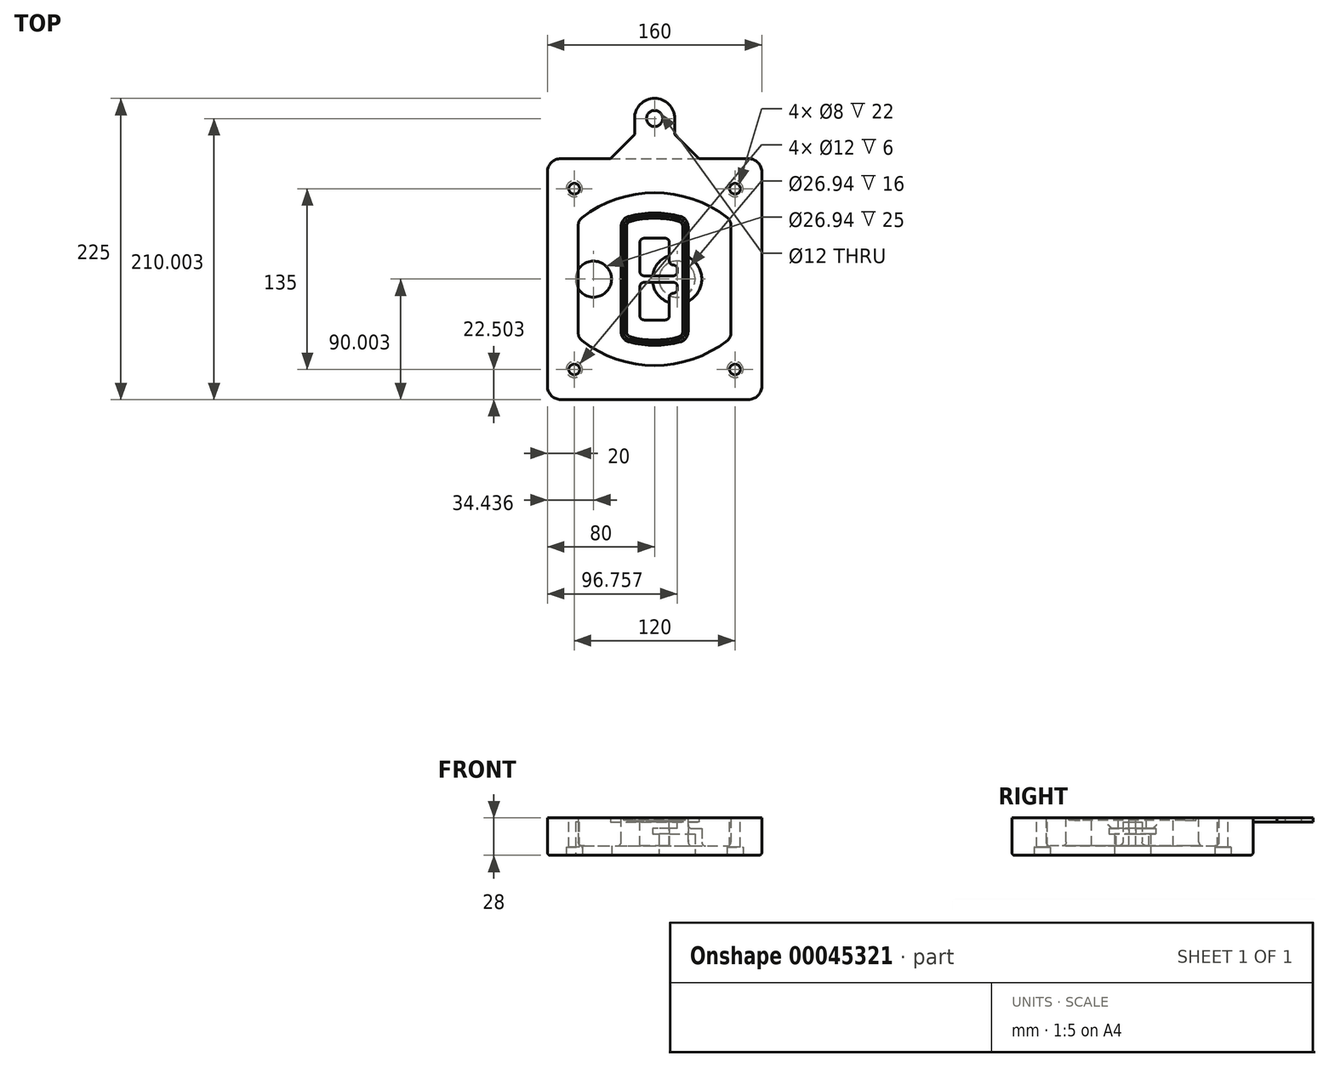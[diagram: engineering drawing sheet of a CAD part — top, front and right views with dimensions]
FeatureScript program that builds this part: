
annotation { "Feature Type Name" : "Feature", "Feature Type Description" : "" }
export const myFeature = defineFeature(function(context is Context, id is Id, definition is map)
    precondition{}
    {
        {
            var Q0;
            Q0=qCreatedBy(makeId("Top.planeOp"),FACE);
            var sketch = newSketch(context, id + "F0", { "sketchPlane" : qUnion([Q0])});
            skPoint(sketch, "E0.rect.middle", {"position": v(0, 0) * mm});
            skLineSegment(sketch, "E1.bottom", {"start": v(24.05, 28.38) * mm, "end": v(164.05, 28.38) * mm});
            skLineSegment(sketch, "E1.top", {"start": v(24.05, 208.38) * mm, "end": v(164.05, 208.38) * mm});
            skLineSegment(sketch, "E1.left", {"start": v(14.05, 38.38) * mm, "end": v(14.05, 198.38) * mm});
            skLineSegment(sketch, "E1.right", {"start": v(174.05, 38.38) * mm, "end": v(174.05, 198.38) * mm});
            skLineSegment(sketch, "E2", {"start": v(14.05, 208.38) * mm, "end": v(174.05, 28.38) * mm, "construction": true});
            skLineSegment(sketch, "E3", {"start": v(174.05, 208.38) * mm, "end": v(14.05, 28.38) * mm, "construction": true});
            skCircle(sketch, "E4", {"center": v(34.05, 185.88) * mm, "radius": 4 * mm});
            skCircle(sketch, "E5", {"center": v(154.05, 185.88) * mm, "radius": 4 * mm});
            skCircle(sketch, "E6", {"center": v(154.05, 50.88) * mm, "radius": 4 * mm});
            skCircle(sketch, "E7", {"center": v(34.05, 50.88) * mm, "radius": 4 * mm});
            skLineSegment(sketch, "E8", {"start": v(34.05, 185.88) * mm, "end": v(154.05, 185.88) * mm, "construction": true});
            skLineSegment(sketch, "E9", {"start": v(154.05, 185.88) * mm, "end": v(154.05, 50.88) * mm, "construction": true});
            skLineSegment(sketch, "E10", {"start": v(154.05, 50.88) * mm, "end": v(34.05, 50.88) * mm, "construction": true});
            skLineSegment(sketch, "E11", {"start": v(34.05, 50.88) * mm, "end": v(34.05, 185.88) * mm, "construction": true});
            skLineSegment(sketch, "E12", {"start": v(34.05, 158.68) * mm, "end": v(34.05, 78.09) * mm});
            skLineSegment(sketch, "E13", {"start": v(154.05, 158.68) * mm, "end": v(154.05, 78.09) * mm});
            skArc(sketch, "E14", {"start": v(150.2, 166.56) * mm, "mid": v(94.05, 185.88) * mm, "end": v(37.9, 166.56) * mm});
            skArc(sketch, "E15", {"start": v(37.9, 70.2) * mm, "mid": v(94.05, 50.88) * mm, "end": v(150.2, 70.2) * mm});
            skLineSegment(sketch, "E16", {"start": v(34.05, 118.38) * mm, "end": v(154.05, 118.38) * mm, "construction": true});
            skPoint(sketch, "E17.visualSharp", {"position": v(34.05, 73.38) * mm});
            skArc(sketch, "E17.filletArc", {"start": v(34.05, 78.09) * mm, "mid": v(35.06, 73.7) * mm, "end": v(37.9, 70.2) * mm});
            skPoint(sketch, "E18.visualSharp", {"position": v(34.05, 163.38) * mm});
            skArc(sketch, "E18.filletArc", {"start": v(37.9, 166.56) * mm, "mid": v(35.06, 163.06) * mm, "end": v(34.05, 158.68) * mm});
            skPoint(sketch, "E19.visualSharp", {"position": v(154.05, 163.38) * mm});
            skArc(sketch, "E19.filletArc", {"start": v(154.05, 158.68) * mm, "mid": v(153.04, 163.06) * mm, "end": v(150.2, 166.56) * mm});
            skPoint(sketch, "E20.visualSharp", {"position": v(154.05, 73.38) * mm});
            skArc(sketch, "E20.filletArc", {"start": v(150.2, 70.2) * mm, "mid": v(153.04, 73.7) * mm, "end": v(154.05, 78.09) * mm});
            skPoint(sketch, "E21.visualSharp", {"position": v(14.05, 208.38) * mm});
            skArc(sketch, "E21.filletArc", {"start": v(24.05, 208.38) * mm, "mid": v(16.98, 205.45) * mm, "end": v(14.05, 198.38) * mm});
            skPoint(sketch, "E22.visualSharp", {"position": v(174.05, 208.38) * mm});
            skArc(sketch, "E22.filletArc", {"start": v(174.05, 198.38) * mm, "mid": v(171.12, 205.45) * mm, "end": v(164.05, 208.38) * mm});
            skPoint(sketch, "E23.visualSharp", {"position": v(174.05, 28.38) * mm});
            skArc(sketch, "E23.filletArc", {"start": v(164.05, 28.38) * mm, "mid": v(171.12, 31.31) * mm, "end": v(174.05, 38.38) * mm});
            skPoint(sketch, "E24.visualSharp", {"position": v(14.05, 28.38) * mm});
            skArc(sketch, "E24.filletArc", {"start": v(14.05, 38.38) * mm, "mid": v(16.98, 31.31) * mm, "end": v(24.05, 28.38) * mm});
            skArc(sketch, "E25.0", {"start": v(151.05, 158.68) * mm, "mid": v(150.34, 161.75) * mm, "end": v(148.36, 164.2) * mm});
            skLineSegment(sketch, "E25.1", {"start": v(151.05, 158.68) * mm, "end": v(151.05, 78.09) * mm});
            skArc(sketch, "E25.2", {"start": v(148.36, 72.57) * mm, "mid": v(150.34, 75.02) * mm, "end": v(151.05, 78.09) * mm});
            skArc(sketch, "E25.3", {"start": v(39.74, 72.57) * mm, "mid": v(94.05, 53.88) * mm, "end": v(148.36, 72.57) * mm});
            skArc(sketch, "E25.4", {"start": v(37.05, 78.09) * mm, "mid": v(37.76, 75.02) * mm, "end": v(39.74, 72.57) * mm});
            skArc(sketch, "E25.5", {"start": v(148.36, 164.2) * mm, "mid": v(94.05, 182.88) * mm, "end": v(39.74, 164.2) * mm});
            skLineSegment(sketch, "E25.6", {"start": v(37.05, 158.68) * mm, "end": v(37.05, 78.09) * mm});
            skArc(sketch, "E25.7", {"start": v(39.74, 164.2) * mm, "mid": v(37.76, 161.75) * mm, "end": v(37.05, 158.68) * mm});
            skArc(sketch, "E26.0", {"start": v(35.43, 169.71) * mm, "mid": v(31.47, 164.82) * mm, "end": v(30.05, 158.68) * mm});
            skArc(sketch, "E26.1", {"start": v(152.67, 169.71) * mm, "mid": v(94.05, 189.88) * mm, "end": v(35.43, 169.71) * mm});
            skArc(sketch, "E26.2", {"start": v(158.05, 158.68) * mm, "mid": v(156.63, 164.82) * mm, "end": v(152.67, 169.71) * mm});
            skLineSegment(sketch, "E26.3", {"start": v(158.05, 158.68) * mm, "end": v(158.05, 78.09) * mm});
            skArc(sketch, "E26.4", {"start": v(152.67, 67.05) * mm, "mid": v(156.63, 71.95) * mm, "end": v(158.05, 78.09) * mm});
            skLineSegment(sketch, "E26.5", {"start": v(30.05, 158.68) * mm, "end": v(30.05, 78.09) * mm});
            skArc(sketch, "E26.6", {"start": v(35.43, 67.05) * mm, "mid": v(94.05, 46.88) * mm, "end": v(152.67, 67.05) * mm});
            skArc(sketch, "E26.7", {"start": v(30.05, 78.09) * mm, "mid": v(31.47, 71.95) * mm, "end": v(35.43, 67.05) * mm});
            skSolve(sketch);
        }
        {
            var Q0;
            Q0=makeQuery(id+"F0.imprint","IMPRINT",FACE,{"disambiguationData":[TD([[makeQuery(id+"F0.imprint","IMPRINT",EDGE,{"derivedFrom":sQuery(id+"F0.wireOp",EDGE,"E1.bottom")}),1.0]])]});
            var Q1;
            Q1=makeQuery(id+"F0.imprint","IMPRINT",FACE,{"disambiguationData":[TD([[makeQuery(id+"F0.imprint","IMPRINT",EDGE,{"derivedFrom":sQuery(id+"F0.wireOp",EDGE,"E12")}),1.0]])]});
            var Q2;
            Q2=makeQuery(id+"F0.imprint","IMPRINT",FACE,{"disambiguationData":[TD([[makeQuery(id+"F0.imprint","IMPRINT",EDGE,{"derivedFrom":sQuery(id+"F0.wireOp",EDGE,"E25.0")}),1.0]])]});
            var Q3;
            Q3=makeQuery(id+"F0.imprint","IMPRINT",FACE,{"disambiguationData":[TD([[makeQuery(id+"F0.imprint","IMPRINT",EDGE,{"derivedFrom":sQuery(id+"F0.wireOp",EDGE,"E12")}),-1.0]])]});
            extrude(context, id + "F1", {"entities" : qUnion([Q0, Q1, Q2, Q3]), "oppositeDirection" : true, "depth" : 25 * mm});
        }
        {
            var Q0;
            Q0=makeQuery(id+"F0.imprint","IMPRINT",FACE,{"disambiguationData":[TD([[makeQuery(id+"F0.imprint","IMPRINT",EDGE,{"derivedFrom":sQuery(id+"F0.wireOp",EDGE,"E12")}),1.0]])]});
            extrude(context, id + "F2", {"entities" : qUnion([Q0]), "operationType" : NewBodyOperationType.ADD, "depth" : 3 * mm});
        }
        {
            var Q0;
            Q0=makeQuery(id+"F0.imprint","IMPRINT",FACE,{"disambiguationData":[TD([[makeQuery(id+"F0.imprint","IMPRINT",EDGE,{"derivedFrom":sQuery(id+"F0.wireOp",EDGE,"E25.0")}),1.0]])]});
            extrude(context, id + "F3", {"entities" : qUnion([Q0]), "operationType" : NewBodyOperationType.REMOVE, "oppositeDirection" : true, "depth" : 18 * mm});
        }
        {
            var Q0;
            Q0=makeQuery(id+"F2.opExtrude","CAP_FACE",FACE,{"disambiguationData":[OSD([sQuery(id+"F0.wireOp",EDGE,"E12"),sQuery(id+"F0.wireOp",EDGE,"E13"),sQuery(id+"F0.wireOp",EDGE,"E14"),sQuery(id+"F0.wireOp",EDGE,"E15"),sQuery(id+"F0.wireOp",EDGE,"E17.filletArc"),sQuery(id+"F0.wireOp",EDGE,"E18.filletArc"),sQuery(id+"F0.wireOp",EDGE,"E19.filletArc"),sQuery(id+"F0.wireOp",EDGE,"E20.filletArc"),sQuery(id+"F0.wireOp",EDGE,"E25.0"),sQuery(id+"F0.wireOp",EDGE,"E25.1"),sQuery(id+"F0.wireOp",EDGE,"E25.2"),sQuery(id+"F0.wireOp",EDGE,"E25.3"),sQuery(id+"F0.wireOp",EDGE,"E25.4"),sQuery(id+"F0.wireOp",EDGE,"E25.5"),sQuery(id+"F0.wireOp",EDGE,"E25.6"),sQuery(id+"F0.wireOp",EDGE,"E25.7")])],"isStart":false});
            var sketch = newSketch(context, id + "F4", { "sketchPlane" : qUnion([Q0])});
            skArc(sketch, "E27.0", {"start": v(74.97, 71.41) * mm, "mid": v(94.05, 68.88) * mm, "end": v(113.13, 71.41) * mm});
            skArc(sketch, "E28.0", {"start": v(113.13, 165.35) * mm, "mid": v(94.05, 167.88) * mm, "end": v(74.97, 165.35) * mm});
            skLineSegment(sketch, "E29", {"start": v(69.05, 157.63) * mm, "end": v(69.05, 79.14) * mm});
            skLineSegment(sketch, "E30", {"start": v(119.05, 157.63) * mm, "end": v(119.05, 79.14) * mm});
            skLineSegment(sketch, "E31", {"start": v(69.05, 163.48) * mm, "end": v(119.05, 163.48) * mm, "construction": true});
            skLineSegment(sketch, "E32", {"start": v(69.05, 73.28) * mm, "end": v(119.05, 73.28) * mm, "construction": true});
            skPoint(sketch, "E33.visualSharp", {"position": v(69.05, 163.48) * mm});
            skArc(sketch, "E33.filletArc", {"start": v(74.97, 165.35) * mm, "mid": v(70.7, 162.5) * mm, "end": v(69.05, 157.63) * mm});
            skPoint(sketch, "E34.visualSharp", {"position": v(119.05, 163.48) * mm});
            skArc(sketch, "E34.filletArc", {"start": v(119.05, 157.63) * mm, "mid": v(117.4, 162.5) * mm, "end": v(113.13, 165.35) * mm});
            skPoint(sketch, "E35.visualSharp", {"position": v(119.05, 73.28) * mm});
            skArc(sketch, "E35.filletArc", {"start": v(113.13, 71.41) * mm, "mid": v(117.4, 74.27) * mm, "end": v(119.05, 79.14) * mm});
            skPoint(sketch, "E36.visualSharp", {"position": v(69.05, 73.28) * mm});
            skArc(sketch, "E36.filletArc", {"start": v(69.05, 79.14) * mm, "mid": v(70.7, 74.27) * mm, "end": v(74.97, 71.41) * mm});
            skArc(sketch, "E37.0", {"start": v(148.36, 164.2) * mm, "mid": v(94.05, 182.88) * mm, "end": v(39.74, 164.2) * mm});
            skArc(sketch, "E37.1", {"start": v(39.74, 164.2) * mm, "mid": v(37.76, 161.75) * mm, "end": v(37.05, 158.68) * mm});
            skLineSegment(sketch, "E37.2", {"start": v(37.05, 158.68) * mm, "end": v(37.05, 78.09) * mm});
            skArc(sketch, "E37.3", {"start": v(37.05, 78.09) * mm, "mid": v(37.76, 75.02) * mm, "end": v(39.74, 72.57) * mm});
            skArc(sketch, "E37.4", {"start": v(39.74, 72.57) * mm, "mid": v(94.05, 53.88) * mm, "end": v(148.36, 72.57) * mm});
            skArc(sketch, "E37.5", {"start": v(148.36, 72.57) * mm, "mid": v(150.34, 75.02) * mm, "end": v(151.05, 78.09) * mm});
            skLineSegment(sketch, "E37.6", {"start": v(151.05, 158.68) * mm, "end": v(151.05, 78.09) * mm});
            skArc(sketch, "E37.7", {"start": v(151.05, 158.68) * mm, "mid": v(150.34, 161.75) * mm, "end": v(148.36, 164.2) * mm});
            skLineSegment(sketch, "E38.0", {"start": v(117.05, 157.63) * mm, "end": v(117.05, 79.14) * mm});
            skArc(sketch, "E38.1", {"start": v(112.61, 73.34) * mm, "mid": v(115.81, 75.49) * mm, "end": v(117.05, 79.14) * mm});
            skArc(sketch, "E38.2", {"start": v(75.49, 73.34) * mm, "mid": v(94.05, 70.88) * mm, "end": v(112.61, 73.34) * mm});
            skArc(sketch, "E38.3", {"start": v(71.05, 79.14) * mm, "mid": v(72.29, 75.49) * mm, "end": v(75.49, 73.34) * mm});
            skLineSegment(sketch, "E38.4", {"start": v(71.05, 157.63) * mm, "end": v(71.05, 79.14) * mm});
            skArc(sketch, "E38.5", {"start": v(117.05, 157.63) * mm, "mid": v(115.81, 161.28) * mm, "end": v(112.61, 163.42) * mm});
            skArc(sketch, "E38.6", {"start": v(75.49, 163.42) * mm, "mid": v(72.29, 161.28) * mm, "end": v(71.05, 157.63) * mm});
            skArc(sketch, "E38.7", {"start": v(112.61, 163.42) * mm, "mid": v(94.05, 165.88) * mm, "end": v(75.49, 163.42) * mm});
            skArc(sketch, "E39.0", {"start": v(115.05, 157.63) * mm, "mid": v(114.23, 160.06) * mm, "end": v(112.1, 161.5) * mm});
            skLineSegment(sketch, "E39.1", {"start": v(115.05, 157.63) * mm, "end": v(115.05, 79.14) * mm});
            skArc(sketch, "E39.2", {"start": v(112.1, 75.27) * mm, "mid": v(114.23, 76.7) * mm, "end": v(115.05, 79.14) * mm});
            skArc(sketch, "E39.3", {"start": v(76, 75.27) * mm, "mid": v(94.05, 72.88) * mm, "end": v(112.1, 75.27) * mm});
            skArc(sketch, "E39.4", {"start": v(73.05, 79.14) * mm, "mid": v(73.87, 76.7) * mm, "end": v(76, 75.27) * mm});
            skArc(sketch, "E39.5", {"start": v(112.1, 161.5) * mm, "mid": v(94.05, 163.88) * mm, "end": v(76, 161.5) * mm});
            skLineSegment(sketch, "E39.6", {"start": v(73.05, 157.63) * mm, "end": v(73.05, 79.14) * mm});
            skArc(sketch, "E39.7", {"start": v(76, 161.5) * mm, "mid": v(73.87, 160.06) * mm, "end": v(73.05, 157.63) * mm});
            skLineSegment(sketch, "E40", {"start": v(69.05, 118.38) * mm, "end": v(119.05, 118.38) * mm, "construction": true});
            skLineSegment(sketch, "E41", {"start": v(83.05, 123.88) * mm, "end": v(83.05, 145.88) * mm});
            skLineSegment(sketch, "E42", {"start": v(86.05, 148.88) * mm, "end": v(102.05, 148.88) * mm});
            skLineSegment(sketch, "E43", {"start": v(105.05, 145.88) * mm, "end": v(105.05, 131.88) * mm});
            skLineSegment(sketch, "E44", {"start": v(108.05, 128.88) * mm, "end": v(108.05, 128.88) * mm});
            skLineSegment(sketch, "E45", {"start": v(111.05, 125.88) * mm, "end": v(111.05, 123.88) * mm});
            skLineSegment(sketch, "E46", {"start": v(108.05, 120.88) * mm, "end": v(86.05, 120.88) * mm});
            skPoint(sketch, "E47.visualSharp", {"position": v(83.05, 148.88) * mm});
            skArc(sketch, "E47.filletArc", {"start": v(86.05, 148.88) * mm, "mid": v(83.93, 148) * mm, "end": v(83.05, 145.88) * mm});
            skPoint(sketch, "E48.visualSharp", {"position": v(105.05, 148.88) * mm});
            skArc(sketch, "E48.filletArc", {"start": v(105.05, 145.88) * mm, "mid": v(104.17, 148) * mm, "end": v(102.05, 148.88) * mm});
            skPoint(sketch, "E49.visualSharp", {"position": v(105.05, 128.88) * mm});
            skArc(sketch, "E49.filletArc", {"start": v(105.05, 131.88) * mm, "mid": v(105.93, 129.76) * mm, "end": v(108.05, 128.88) * mm});
            skPoint(sketch, "E50.visualSharp", {"position": v(111.05, 128.88) * mm});
            skArc(sketch, "E50.filletArc", {"start": v(111.05, 125.88) * mm, "mid": v(110.17, 128) * mm, "end": v(108.05, 128.88) * mm});
            skPoint(sketch, "E51.visualSharp", {"position": v(111.05, 120.88) * mm});
            skArc(sketch, "E51.filletArc", {"start": v(108.05, 120.88) * mm, "mid": v(110.17, 121.76) * mm, "end": v(111.05, 123.88) * mm});
            skPoint(sketch, "E52.visualSharp", {"position": v(83.05, 120.88) * mm});
            skArc(sketch, "E52.filletArc", {"start": v(83.05, 123.88) * mm, "mid": v(83.93, 121.76) * mm, "end": v(86.05, 120.88) * mm});
            skLineSegment(sketch, "E53.0.MirrorCS", {"start": v(108.05, 115.88) * mm, "end": v(86.05, 115.88) * mm});
            skArc(sketch, "E54.0.MirrorCS", {"start": v(83.05, 112.88) * mm, "mid": v(83.93, 115) * mm, "end": v(86.05, 115.88) * mm});
            skLineSegment(sketch, "E55.0.MirrorCS", {"start": v(83.05, 112.88) * mm, "end": v(83.05, 90.88) * mm});
            skArc(sketch, "E56.0.MirrorCS", {"start": v(86.05, 87.88) * mm, "mid": v(83.93, 88.76) * mm, "end": v(83.05, 90.88) * mm});
            skLineSegment(sketch, "E57.0.MirrorCS", {"start": v(86.05, 87.88) * mm, "end": v(102.05, 87.88) * mm});
            skArc(sketch, "E58.0.MirrorCS", {"start": v(105.05, 90.88) * mm, "mid": v(104.17, 88.76) * mm, "end": v(102.05, 87.88) * mm});
            skLineSegment(sketch, "E59.0.MirrorCS", {"start": v(105.05, 90.88) * mm, "end": v(105.05, 104.88) * mm});
            skArc(sketch, "E60.0.MirrorCS", {"start": v(105.05, 104.88) * mm, "mid": v(105.93, 107) * mm, "end": v(108.05, 107.88) * mm});
            skArc(sketch, "E61.0.MirrorCS", {"start": v(111.05, 110.88) * mm, "mid": v(110.17, 108.76) * mm, "end": v(108.05, 107.88) * mm});
            skLineSegment(sketch, "E62.0.MirrorCS", {"start": v(111.05, 110.88) * mm, "end": v(111.05, 112.88) * mm});
            skArc(sketch, "E63.0.MirrorCS", {"start": v(108.05, 115.88) * mm, "mid": v(110.17, 115) * mm, "end": v(111.05, 112.88) * mm});
            skSolve(sketch);
        }
        {
            var Q0;
            Q0=makeQuery(id+"F4.imprint","IMPRINT",FACE,{"disambiguationData":[TD([[makeQuery(id+"F4.imprint","IMPRINT",EDGE,{"derivedFrom":sQuery(id+"F4.wireOp",EDGE,"E27.0")}),1.0]])]});
            var Q1;
            Q1=makeQuery(id+"F4.imprint","IMPRINT",FACE,{"disambiguationData":[TD([[makeQuery(id+"F4.imprint","IMPRINT",EDGE,{"derivedFrom":sQuery(id+"F4.wireOp",EDGE,"E38.0")}),-1.0]])]});
            var Q2;
            Q2=makeQuery(id+"F4.imprint","IMPRINT",FACE,{"disambiguationData":[TD([[makeQuery(id+"F4.imprint","IMPRINT",EDGE,{"derivedFrom":sQuery(id+"F4.wireOp",EDGE,"E39.0")}),1.0]])]});
            extrude(context, id + "F5", {"entities" : qUnion([Q0, Q1, Q2]), "operationType" : NewBodyOperationType.ADD, "endBound" : BoundingType.UP_TO_NEXT, "oppositeDirection" : true, "depth" : 25 * mm});
        }
        {
            var Q0;
            Q0=makeQuery(id+"F4.imprint","IMPRINT",FACE,{"disambiguationData":[TD([[makeQuery(id+"F4.imprint","IMPRINT",EDGE,{"derivedFrom":sQuery(id+"F4.wireOp",EDGE,"E38.0")}),-1.0]])]});
            extrude(context, id + "F6", {"entities" : qUnion([Q0]), "operationType" : NewBodyOperationType.REMOVE, "oppositeDirection" : true, "depth" : 2 * mm});
        }
        {
            var Q0;
            Q0=makeQuery(id+"F1.opExtrude","CAP_FACE",FACE,{"disambiguationData":[OSD([sQuery(id+"F0.wireOp",EDGE,"E1.bottom"),sQuery(id+"F0.wireOp",EDGE,"E1.top"),sQuery(id+"F0.wireOp",EDGE,"E1.left"),sQuery(id+"F0.wireOp",EDGE,"E1.right"),sQuery(id+"F0.wireOp",EDGE,"E4"),sQuery(id+"F0.wireOp",EDGE,"E5"),sQuery(id+"F0.wireOp",EDGE,"E6"),sQuery(id+"F0.wireOp",EDGE,"E7"),sQuery(id+"F0.wireOp",EDGE,"E21.filletArc"),sQuery(id+"F0.wireOp",EDGE,"E22.filletArc"),sQuery(id+"F0.wireOp",EDGE,"E23.filletArc"),sQuery(id+"F0.wireOp",EDGE,"E24.filletArc")])],"isStart":false});
            var sketch = newSketch(context, id + "F7", { "sketchPlane" : qUnion([Q0])});
            skCircle(sketch, "E64", {"center": v(110.8, -118.38) * mm, "radius": 13.47 * mm});
            skCircle(sketch, "E65", {"center": v(48.49, -118.38) * mm, "radius": 13.47 * mm});
            skLineSegment(sketch, "E66", {"start": v(174.05, -118.38) * mm, "end": v(14.05, -118.38) * mm});
            skCircle(sketch, "E67", {"center": v(110.8, -118.38) * mm, "radius": 18.47 * mm});
            skCircle(sketch, "E68", {"center": v(154.05, -185.88) * mm, "radius": 6 * mm});
            skCircle(sketch, "E69", {"center": v(34.05, -185.88) * mm, "radius": 6 * mm});
            skCircle(sketch, "E70", {"center": v(34.05, -50.88) * mm, "radius": 6 * mm});
            skCircle(sketch, "E71", {"center": v(154.05, -50.88) * mm, "radius": 6 * mm});
            skSolve(sketch);
        }
        {
            var Q0;
            {var subQ1=sQuery(id+"F7.wireOp",EDGE,"E66");var subQ4=sQuery(id+"F7.wireOp",EDGE,"E64");var subQ6=makeQuery(id+"F7.imprint","INTERSECT",VERTEX,{"disambiguationData":[OD(0.0)],"derivedFrom":[subQ4,subQ1]});Q0=makeQuery(id+"F7.imprint","IMPRINT",FACE,{"disambiguationData":[TD([[makeQuery(id+"F7.imprint","IMPRINT",EDGE,{"disambiguationData":[TD([[subQ6,-1.0]])],"derivedFrom":subQ4}),-1.0]])]});}
            var Q1;
            {var subQ0=sQuery(id+"F7.wireOp",EDGE,"E66");var subQ1=sQuery(id+"F7.wireOp",EDGE,"E64");var subQ3=makeQuery(id+"F7.imprint","INTERSECT",VERTEX,{"disambiguationData":[OD(0.0)],"derivedFrom":[subQ1,subQ0]});Q1=makeQuery(id+"F7.imprint","IMPRINT",FACE,{"disambiguationData":[TD([[makeQuery(id+"F7.imprint","IMPRINT",EDGE,{"disambiguationData":[TD([[subQ3,-1.0]])],"derivedFrom":subQ1}),1.0]])]});}
            var Q2;
            {var subQ0=sQuery(id+"F7.wireOp",EDGE,"E66");var subQ1=sQuery(id+"F7.wireOp",EDGE,"E64");var subQ3=makeQuery(id+"F7.imprint","INTERSECT",VERTEX,{"disambiguationData":[OD(0.0)],"derivedFrom":[subQ1,subQ0]});Q2=makeQuery(id+"F7.imprint","IMPRINT",FACE,{"disambiguationData":[TD([[makeQuery(id+"F7.imprint","IMPRINT",EDGE,{"disambiguationData":[TD([[subQ3,1.0]])],"derivedFrom":subQ1}),1.0]])]});}
            var Q3;
            {var subQ1=sQuery(id+"F7.wireOp",EDGE,"E66");var subQ4=sQuery(id+"F7.wireOp",EDGE,"E64");var subQ6=makeQuery(id+"F7.imprint","INTERSECT",VERTEX,{"disambiguationData":[OD(0.0)],"derivedFrom":[subQ4,subQ1]});Q3=makeQuery(id+"F7.imprint","IMPRINT",FACE,{"disambiguationData":[TD([[makeQuery(id+"F7.imprint","IMPRINT",EDGE,{"disambiguationData":[TD([[subQ6,1.0]])],"derivedFrom":subQ4}),-1.0]])]});}
            extrude(context, id + "F8", {"entities" : qUnion([Q0, Q1, Q2, Q3]), "operationType" : NewBodyOperationType.ADD, "oppositeDirection" : true, "depth" : 20 * mm});
        }
        {
            var Q0;
            {var subQ0=sQuery(id+"F7.wireOp",EDGE,"E66");var subQ1=sQuery(id+"F7.wireOp",EDGE,"E64");var subQ3=makeQuery(id+"F7.imprint","INTERSECT",VERTEX,{"disambiguationData":[OD(0.0)],"derivedFrom":[subQ1,subQ0]});Q0=makeQuery(id+"F7.imprint","IMPRINT",FACE,{"disambiguationData":[TD([[makeQuery(id+"F7.imprint","IMPRINT",EDGE,{"disambiguationData":[TD([[subQ3,-1.0]])],"derivedFrom":subQ1}),1.0]])]});}
            var Q1;
            {var subQ0=sQuery(id+"F7.wireOp",EDGE,"E66");var subQ1=sQuery(id+"F7.wireOp",EDGE,"E64");var subQ3=makeQuery(id+"F7.imprint","INTERSECT",VERTEX,{"disambiguationData":[OD(0.0)],"derivedFrom":[subQ1,subQ0]});Q1=makeQuery(id+"F7.imprint","IMPRINT",FACE,{"disambiguationData":[TD([[makeQuery(id+"F7.imprint","IMPRINT",EDGE,{"disambiguationData":[TD([[subQ3,1.0]])],"derivedFrom":subQ1}),1.0]])]});}
            extrude(context, id + "F9", {"entities" : qUnion([Q0, Q1]), "operationType" : NewBodyOperationType.REMOVE, "oppositeDirection" : true, "depth" : 16 * mm});
        }
        {
            var Q0;
            {var subQ0=sQuery(id+"F7.wireOp",EDGE,"E66");var subQ1=sQuery(id+"F7.wireOp",EDGE,"E65");var subQ3=makeQuery(id+"F7.imprint","INTERSECT",VERTEX,{"disambiguationData":[OD(0.0)],"derivedFrom":[subQ1,subQ0]});Q0=makeQuery(id+"F7.imprint","IMPRINT",FACE,{"disambiguationData":[TD([[makeQuery(id+"F7.imprint","IMPRINT",EDGE,{"disambiguationData":[TD([[subQ3,-1.0]])],"derivedFrom":subQ1}),1.0]])]});}
            var Q1;
            {var subQ0=sQuery(id+"F7.wireOp",EDGE,"E66");var subQ1=sQuery(id+"F7.wireOp",EDGE,"E65");var subQ3=makeQuery(id+"F7.imprint","INTERSECT",VERTEX,{"disambiguationData":[OD(0.0)],"derivedFrom":[subQ1,subQ0]});Q1=makeQuery(id+"F7.imprint","IMPRINT",FACE,{"disambiguationData":[TD([[makeQuery(id+"F7.imprint","IMPRINT",EDGE,{"disambiguationData":[TD([[subQ3,1.0]])],"derivedFrom":subQ1}),1.0]])]});}
            extrude(context, id + "F10", {"entities" : qUnion([Q0, Q1]), "operationType" : NewBodyOperationType.REMOVE, "oppositeDirection" : true, "depth" : 25 * mm});
        }
        {
            var Q0;
            Q0=makeQuery(id+"F7.imprint","IMPRINT",FACE,{"disambiguationData":[TD([[makeQuery(id+"F7.imprint","IMPRINT",EDGE,{"derivedFrom":sQuery(id+"F7.wireOp",EDGE,"E68")}),1.0]])]});
            var Q1;
            Q1=makeQuery(id+"F7.imprint","IMPRINT",FACE,{"disambiguationData":[TD([[makeQuery(id+"F7.imprint","IMPRINT",EDGE,{"derivedFrom":makeQuery(id+"F1.opExtrude","CAP_EDGE",EDGE,{"disambiguationData":[OSD([sQuery(id+"F0.wireOp",EDGE,"E5")])],"isStart":false})}),-1.0]])]});
            var Q2;
            Q2=makeQuery(id+"F7.imprint","IMPRINT",FACE,{"disambiguationData":[TD([[makeQuery(id+"F7.imprint","IMPRINT",EDGE,{"derivedFrom":sQuery(id+"F7.wireOp",EDGE,"E69")}),1.0]])]});
            var Q3;
            Q3=makeQuery(id+"F7.imprint","IMPRINT",FACE,{"disambiguationData":[TD([[makeQuery(id+"F7.imprint","IMPRINT",EDGE,{"derivedFrom":makeQuery(id+"F1.opExtrude","CAP_EDGE",EDGE,{"disambiguationData":[OSD([sQuery(id+"F0.wireOp",EDGE,"E4")])],"isStart":false})}),-1.0]])]});
            var Q4;
            Q4=makeQuery(id+"F7.imprint","IMPRINT",FACE,{"disambiguationData":[TD([[makeQuery(id+"F7.imprint","IMPRINT",EDGE,{"derivedFrom":sQuery(id+"F7.wireOp",EDGE,"E70")}),1.0]])]});
            var Q5;
            Q5=makeQuery(id+"F7.imprint","IMPRINT",FACE,{"disambiguationData":[TD([[makeQuery(id+"F7.imprint","IMPRINT",EDGE,{"derivedFrom":makeQuery(id+"F1.opExtrude","CAP_EDGE",EDGE,{"disambiguationData":[OSD([sQuery(id+"F0.wireOp",EDGE,"E7")])],"isStart":false})}),-1.0]])]});
            var Q6;
            Q6=makeQuery(id+"F7.imprint","IMPRINT",FACE,{"disambiguationData":[TD([[makeQuery(id+"F7.imprint","IMPRINT",EDGE,{"derivedFrom":sQuery(id+"F7.wireOp",EDGE,"E71")}),1.0]])]});
            var Q7;
            Q7=makeQuery(id+"F7.imprint","IMPRINT",FACE,{"disambiguationData":[TD([[makeQuery(id+"F7.imprint","IMPRINT",EDGE,{"derivedFrom":makeQuery(id+"F1.opExtrude","CAP_EDGE",EDGE,{"disambiguationData":[OSD([sQuery(id+"F0.wireOp",EDGE,"E6")])],"isStart":false})}),-1.0]])]});
            extrude(context, id + "F11", {"entities" : qUnion([Q0, Q1, Q2, Q3, Q4, Q5, Q6, Q7]), "operationType" : NewBodyOperationType.REMOVE, "oppositeDirection" : true, "depth" : 6 * mm});
        }
        {
            var Q0;
            Q0=makeQuery(id+"F9.boolean.opBoolean","COPY",FACE,{"derivedFrom":makeQuery(id+"F9.opExtrude","CAP_FACE",FACE,{"disambiguationData":[OSD([sQuery(id+"F7.wireOp",EDGE,"E64")])],"isStart":false})});
            var sketch = newSketch(context, id + "F12", { "sketchPlane" : qUnion([Q0])});
            skArc(sketch, "E72.0", {"start": v(105.05, -100.83) * mm, "mid": v(96.62, -106.56) * mm, "end": v(92.5, -115.88) * mm});
            skArc(sketch, "E72.1", {"start": v(92.5, -120.88) * mm, "mid": v(96.62, -130.2) * mm, "end": v(105.05, -135.93) * mm});
            skLineSegment(sketch, "E73", {"start": v(92.5, -120.88) * mm, "end": v(108.05, -120.88) * mm});
            skLineSegment(sketch, "E74.0", {"start": v(108.05, -115.88) * mm, "end": v(92.5, -115.88) * mm});
            skArc(sketch, "E74.1", {"start": v(108.05, -115.88) * mm, "mid": v(110.17, -115) * mm, "end": v(111.05, -112.88) * mm});
            skLineSegment(sketch, "E74.2", {"start": v(111.05, -110.88) * mm, "end": v(111.05, -112.88) * mm});
            skArc(sketch, "E74.3", {"start": v(111.05, -110.88) * mm, "mid": v(110.17, -108.76) * mm, "end": v(108.05, -107.88) * mm});
            skArc(sketch, "E74.4", {"start": v(105.05, -104.88) * mm, "mid": v(105.93, -107) * mm, "end": v(108.05, -107.88) * mm});
            skLineSegment(sketch, "E74.5", {"start": v(105.05, -100.83) * mm, "end": v(105.05, -104.88) * mm});
            skLineSegment(sketch, "E74.7", {"start": v(108.05, -120.88) * mm, "end": v(92.5, -120.88) * mm});
            skArc(sketch, "E74.8", {"start": v(108.05, -120.88) * mm, "mid": v(110.17, -121.76) * mm, "end": v(111.05, -123.88) * mm});
            skLineSegment(sketch, "E74.9", {"start": v(111.05, -125.88) * mm, "end": v(111.05, -123.88) * mm});
            skArc(sketch, "E74.10", {"start": v(111.05, -125.88) * mm, "mid": v(110.17, -128) * mm, "end": v(108.05, -128.88) * mm});
            skArc(sketch, "E74.11", {"start": v(105.05, -131.88) * mm, "mid": v(105.93, -129.76) * mm, "end": v(108.05, -128.88) * mm});
            skLineSegment(sketch, "E74.12", {"start": v(105.05, -135.93) * mm, "end": v(105.05, -131.88) * mm});
            skPoint(sketch, "E75.orphan", {"position": v(105.05, -145.88) * mm});
            skPoint(sketch, "E76.orphan", {"position": v(86.05, -120.88) * mm});
            skPoint(sketch, "E77.orphan", {"position": v(86.05, -115.88) * mm});
            skPoint(sketch, "E78.orphan", {"position": v(105.05, -90.88) * mm});
            skSolve(sketch);
        }
        {
            var Q0;
            {var subQ7=sQuery(id+"F12.wireOp",EDGE,"E72.0");var subQ14=sQuery(id+"F12.wireOp",EDGE,"E72.1");var subQ16=sQuery(id+"F12.wireOp",EDGE,"E74.1");var subQ18=sQuery(id+"F12.wireOp",EDGE,"E74.8");Q0=qUnion([makeQuery(id+"F12.imprint","IMPRINT",FACE,{"disambiguationData":[TD([[makeQuery(id+"F12.imprint","IMPRINT",EDGE,{"derivedFrom":subQ7}),1.0]])]}),makeQuery(id+"F12.imprint","IMPRINT",FACE,{"disambiguationData":[TD([[makeQuery(id+"F12.imprint","IMPRINT",EDGE,{"derivedFrom":subQ14}),1.0]])]}),makeQuery(id+"F12.imprint","IMPRINT",FACE,{"disambiguationData":[TD([[makeQuery(id+"F12.imprint","IMPRINT",EDGE,{"derivedFrom":subQ16}),1.0]])]}),makeQuery(id+"F12.imprint","IMPRINT",FACE,{"disambiguationData":[TD([[makeQuery(id+"F12.imprint","IMPRINT",EDGE,{"derivedFrom":subQ18}),-1.0]])]})]);}
            var Q1;
            Q1=makeQuery(id+"F5.boolean.opBoolean","SPLIT",FACE,{"disambiguationData":[TD([makeQuery(id+"F5.opExtrude","SWEPT_FACE",FACE,{"disambiguationData":[OSD([sQuery(id+"F4.wireOp",EDGE,"E41")])]})])],"derivedFrom":makeQuery(id+"F3.boolean.opBoolean","COPY",FACE,{"derivedFrom":makeQuery(id+"F3.opExtrude","CAP_FACE",FACE,{"disambiguationData":[OSD([sQuery(id+"F0.wireOp",EDGE,"E25.0"),sQuery(id+"F0.wireOp",EDGE,"E25.1"),sQuery(id+"F0.wireOp",EDGE,"E25.2"),sQuery(id+"F0.wireOp",EDGE,"E25.3"),sQuery(id+"F0.wireOp",EDGE,"E25.4"),sQuery(id+"F0.wireOp",EDGE,"E25.5"),sQuery(id+"F0.wireOp",EDGE,"E25.6"),sQuery(id+"F0.wireOp",EDGE,"E25.7")])],"isStart":false})})});
            extrude(context, id + "F13", {"entities" : qUnion([Q0]), "operationType" : NewBodyOperationType.REMOVE, "endBound" : BoundingType.UP_TO_SURFACE, "endBoundEntityFace" : qUnion([Q1]), "depth" : 25 * mm});
        }
        {
            var Q0;
            Q0=makeQuery(id+"F3.boolean.opBoolean","COPY",EDGE,{"derivedFrom":makeQuery(id+"F3.opExtrude","CAP_EDGE",EDGE,{"disambiguationData":[OSD([sQuery(id+"F0.wireOp",EDGE,"E25.6")])],"isStart":false})});
            var Q1;
            Q1=makeQuery(id+"F8.boolean.opBoolean","INTERSECT",EDGE,{"derivedFrom":[makeQuery(id+"F5.opExtrude","SWEPT_FACE",FACE,{"disambiguationData":[OSD([sQuery(id+"F4.wireOp",EDGE,"E30")])]}),makeQuery(id+"F8.opExtrude","CAP_FACE",FACE,{"disambiguationData":[OSD([sQuery(id+"F7.wireOp",EDGE,"E67")])],"isStart":false})]});
            var Q2;
            Q2=makeQuery(id+"F8.boolean.opBoolean","INTERSECT",EDGE,{"disambiguationData":[OD(1.0)],"derivedFrom":[makeQuery(id+"F5.opExtrude","SWEPT_FACE",FACE,{"disambiguationData":[OSD([sQuery(id+"F4.wireOp",EDGE,"E30")])]}),makeQuery(id+"F8.opExtrude","SWEPT_FACE",FACE,{"disambiguationData":[OSD([sQuery(id+"F7.wireOp",EDGE,"E67")])]})]});
            var Q3;
            {var subQ0=sQuery(id+"F4.wireOp",EDGE,"E30");Q3=makeQuery(id+"F8.boolean.opBoolean","SPLIT",EDGE,{"disambiguationData":[TD([makeQuery(id+"F5.opExtrude","SWEPT_FACE",FACE,{"disambiguationData":[OSD([sQuery(id+"F4.wireOp",EDGE,"E35.filletArc")])]})])],"derivedFrom":makeQuery(id+"F5.opExtrude","CAP_EDGE",EDGE,{"disambiguationData":[OSD([subQ0])],"isStart":false})});}
            var Q4;
            {var subQ0=sQuery(id+"F0.wireOp",EDGE,"E25.7");var subQ1=sQuery(id+"F0.wireOp",EDGE,"E25.1");var subQ2=sQuery(id+"F0.wireOp",EDGE,"E25.6");var subQ3=sQuery(id+"F0.wireOp",EDGE,"E25.5");var subQ4=sQuery(id+"F0.wireOp",EDGE,"E25.4");var subQ5=sQuery(id+"F0.wireOp",EDGE,"E25.0");var subQ6=sQuery(id+"F0.wireOp",EDGE,"E25.2");var subQ7=sQuery(id+"F0.wireOp",EDGE,"E25.3");Q4=makeQuery(id+"F8.boolean.opBoolean","INTERSECT",EDGE,{"derivedFrom":[makeQuery(id+"F5.boolean.opBoolean","SPLIT",FACE,{"disambiguationData":[TD([makeQuery(id+"F2.opExtrude","SWEPT_FACE",FACE,{"disambiguationData":[OSD([subQ5])]})])],"derivedFrom":makeQuery(id+"F3.boolean.opBoolean","COPY",FACE,{"derivedFrom":makeQuery(id+"F3.opExtrude","CAP_FACE",FACE,{"disambiguationData":[OSD([subQ5,subQ1,subQ6,subQ7,subQ4,subQ3,subQ2,subQ0])],"isStart":false})})}),makeQuery(id+"F8.opExtrude","SWEPT_FACE",FACE,{"disambiguationData":[OSD([sQuery(id+"F7.wireOp",EDGE,"E67")])]})]});}
            var Q5;
            Q5=makeQuery(id+"F8.boolean.opBoolean","INTERSECT",EDGE,{"disambiguationData":[OD(0.0)],"derivedFrom":[makeQuery(id+"F5.opExtrude","SWEPT_FACE",FACE,{"disambiguationData":[OSD([sQuery(id+"F4.wireOp",EDGE,"E30")])]}),makeQuery(id+"F8.opExtrude","SWEPT_FACE",FACE,{"disambiguationData":[OSD([sQuery(id+"F7.wireOp",EDGE,"E67")])]})]});
            fillet(context, id + "F14", {"entities" : qUnion([Q0, Q1, Q2, Q3, Q4, Q5]), "radius" : 3 * mm, "tangentPropagation" : true, "allowEdgeOverflow" : false});
        }
        {
            var Q0;
            Q0=makeQuery(id+"F1.opExtrude","CAP_EDGE",EDGE,{"disambiguationData":[OSD([sQuery(id+"F0.wireOp",EDGE,"E1.bottom")])],"isStart":false});
            fillet(context, id + "F15", {"entities" : qUnion([Q0]), "radius" : 2 * mm, "tangentPropagation" : true, "allowEdgeOverflow" : false});
        }
        {
            var Q0;
            {var subQ0=sQuery(id+"F0.wireOp",EDGE,"E22.filletArc");var subQ1=sQuery(id+"F0.wireOp",EDGE,"E7");var subQ2=sQuery(id+"F0.wireOp",EDGE,"E6");var subQ3=sQuery(id+"F0.wireOp",EDGE,"E5");var subQ4=sQuery(id+"F0.wireOp",EDGE,"E4");var subQ5=sQuery(id+"F0.wireOp",EDGE,"E1.bottom");var subQ6=sQuery(id+"F0.wireOp",EDGE,"E21.filletArc");var subQ7=sQuery(id+"F0.wireOp",EDGE,"E1.top");var subQ8=sQuery(id+"F0.wireOp",EDGE,"E1.left");var subQ9=sQuery(id+"F0.wireOp",EDGE,"E1.right");var subQ10=sQuery(id+"F0.wireOp",EDGE,"E23.filletArc");var subQ11=sQuery(id+"F0.wireOp",EDGE,"E24.filletArc");Q0=makeQuery(id+"F2.boolean.opBoolean","SPLIT",FACE,{"disambiguationData":[TD([makeQuery(id+"F1.opExtrude","SWEPT_FACE",FACE,{"disambiguationData":[OSD([subQ5])]})])],"derivedFrom":makeQuery(id+"F1.opExtrude","CAP_FACE",FACE,{"disambiguationData":[OSD([subQ5,subQ7,subQ8,subQ9,subQ4,subQ3,subQ2,subQ1,subQ6,subQ0,subQ10,subQ11])],"isStart":true})});}
            var sketch = newSketch(context, id + "F16", { "sketchPlane" : qUnion([Q0])});
            skLineSegment(sketch, "E79", {"start": v(61.05, 208.38) * mm, "end": v(79.05, 226.38) * mm});
            skLineSegment(sketch, "E80", {"start": v(79.05, 226.38) * mm, "end": v(79.05, 238.38) * mm});
            skLineSegment(sketch, "E81", {"start": v(127.05, 208.38) * mm, "end": v(109.05, 226.38) * mm});
            skLineSegment(sketch, "E82", {"start": v(109.05, 226.38) * mm, "end": v(109.05, 238.38) * mm});
            skArc(sketch, "E83", {"start": v(109.05, 238.38) * mm, "mid": v(94.05, 253.38) * mm, "end": v(79.05, 238.38) * mm});
            skCircle(sketch, "E84", {"center": v(94.05, 238.38) * mm, "radius": 6 * mm});
            skLineSegment(sketch, "E85", {"start": v(94.05, 238.38) * mm, "end": v(94.05, 208.38) * mm, "construction": true});
            skLineSegment(sketch, "E86", {"start": v(14.05, 118.38) * mm, "end": v(174.05, 118.38) * mm, "construction": true});
            skArc(sketch, "E87.MirrorCS", {"start": v(79.05, 238.38) * mm, "mid": v(94.05, 253.38) * mm, "end": v(109.05, 238.38) * mm});
            skArc(sketch, "E88.MirrorCS", {"start": v(109.05, -1.62) * mm, "mid": v(94.05, -16.62) * mm, "end": v(79.05, -1.62) * mm});
            skLineSegment(sketch, "E89.MirrorCS", {"start": v(79.05, 10.38) * mm, "end": v(79.05, -1.62) * mm});
            skLineSegment(sketch, "E90.MirrorCS", {"start": v(61.05, 28.38) * mm, "end": v(79.05, 10.38) * mm});
            skLineSegment(sketch, "E91.MirrorCS", {"start": v(127.05, 28.38) * mm, "end": v(109.05, 10.38) * mm});
            skLineSegment(sketch, "E92.MirrorCS", {"start": v(109.05, 10.38) * mm, "end": v(109.05, -1.62) * mm});
            skCircle(sketch, "E93.MirrorC", {"center": v(94.05, -1.62) * mm, "radius": 6 * mm});
            skArc(sketch, "E94.MirrorCS", {"start": v(79.05, -1.62) * mm, "mid": v(94.05, -16.62) * mm, "end": v(109.05, -1.62) * mm});
            skLineSegment(sketch, "E95.MirrorCS", {"start": v(94.05, -1.62) * mm, "end": v(94.05, 28.38) * mm, "construction": true});
            skSolve(sketch);
        }
        {
            var Q0;
            Q0=makeQuery(id+"F16.imprint","IMPRINT",FACE,{"disambiguationData":[TD([[makeQuery(id+"F16.imprint","IMPRINT",EDGE,{"derivedFrom":makeQuery(id+"F1.opExtrude","CAP_EDGE",EDGE,{"disambiguationData":[OSD([sQuery(id+"F0.wireOp",EDGE,"E1.left")])],"isStart":true})}),-1.0]])]});
            var Q1;
            {var subQ0=sQuery(id+"F16.wireOp",EDGE,"E90.MirrorCS");Q1=makeQuery(id+"F16.imprint","IMPRINT",FACE,{"disambiguationData":[TD([[makeQuery(id+"F16.imprint","IMPRINT",EDGE,{"derivedFrom":subQ0}),1.0]])]});}
            var Q2;
            {var subQ1=sQuery(id+"F16.wireOp",EDGE,"E81");Q2=makeQuery(id+"F16.imprint","IMPRINT",FACE,{"disambiguationData":[TD([[makeQuery(id+"F16.imprint","IMPRINT",EDGE,{"derivedFrom":subQ1}),1.0]])]});}
            var Q3;
            Q3=makeQuery(id+"F2.opExtrude","CAP_FACE",FACE,{"disambiguationData":[OSD([sQuery(id+"F0.wireOp",EDGE,"E12"),sQuery(id+"F0.wireOp",EDGE,"E13"),sQuery(id+"F0.wireOp",EDGE,"E14"),sQuery(id+"F0.wireOp",EDGE,"E15"),sQuery(id+"F0.wireOp",EDGE,"E17.filletArc"),sQuery(id+"F0.wireOp",EDGE,"E18.filletArc"),sQuery(id+"F0.wireOp",EDGE,"E19.filletArc"),sQuery(id+"F0.wireOp",EDGE,"E20.filletArc"),sQuery(id+"F0.wireOp",EDGE,"E25.0"),sQuery(id+"F0.wireOp",EDGE,"E25.1"),sQuery(id+"F0.wireOp",EDGE,"E25.2"),sQuery(id+"F0.wireOp",EDGE,"E25.3"),sQuery(id+"F0.wireOp",EDGE,"E25.4"),sQuery(id+"F0.wireOp",EDGE,"E25.5"),sQuery(id+"F0.wireOp",EDGE,"E25.6"),sQuery(id+"F0.wireOp",EDGE,"E25.7")])],"isStart":false});
            extrude(context, id + "F17", {"entities" : qUnion([Q0, Q1, Q2]), "operationType" : NewBodyOperationType.ADD, "endBound" : BoundingType.UP_TO_SURFACE, "endBoundEntityFace" : qUnion([Q3]), "depth" : 25 * mm});
        }
    });
